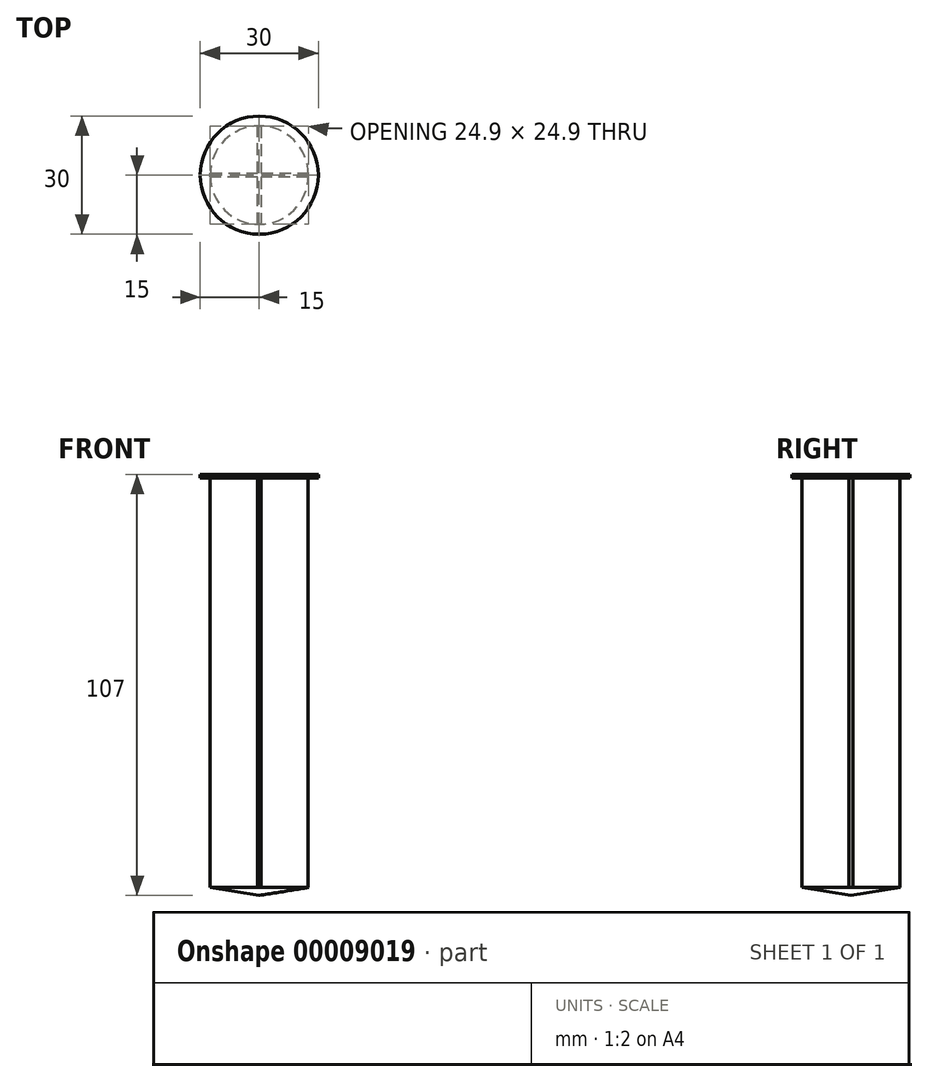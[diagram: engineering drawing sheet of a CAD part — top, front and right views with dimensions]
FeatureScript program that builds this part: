
annotation { "Feature Type Name" : "Feature", "Feature Type Description" : "" }
export const myFeature = defineFeature(function(context is Context, id is Id, definition is map)
    precondition{}
    {
        {
            var Q0;
            Q0=qCreatedBy(makeId("Top.planeOp"),FACE);
            var sketch = newSketch(context, id + "F0", { "sketchPlane" : qUnion([Q0])});
            skLineSegment(sketch, "E0", {"start": v(-0.5, 0.5) * mm, "end": v(-0.5, 12.45) * mm});
            skLineSegment(sketch, "E1", {"start": v(-0.5, 12.45) * mm, "end": v(0.5, 12.45) * mm});
            skLineSegment(sketch, "E2", {"start": v(0.5, 12.45) * mm, "end": v(0.5, 0.5) * mm});
            skLineSegment(sketch, "E3", {"start": v(0.5, 0.5) * mm, "end": v(12.45, 0.5) * mm});
            skLineSegment(sketch, "E4", {"start": v(12.45, 0.5) * mm, "end": v(12.45, -0.5) * mm});
            skLineSegment(sketch, "E5", {"start": v(12.45, -0.5) * mm, "end": v(0.5, -0.5) * mm});
            skLineSegment(sketch, "E6", {"start": v(0.5, -0.5) * mm, "end": v(0.5, -12.45) * mm});
            skLineSegment(sketch, "E7", {"start": v(0.5, -12.45) * mm, "end": v(-0.5, -12.45) * mm});
            skLineSegment(sketch, "E8", {"start": v(-0.5, -12.45) * mm, "end": v(-0.5, -0.5) * mm});
            skLineSegment(sketch, "E9", {"start": v(-0.5, -0.5) * mm, "end": v(-12.45, -0.5) * mm});
            skLineSegment(sketch, "E10", {"start": v(-12.45, -0.5) * mm, "end": v(-12.45, 0.5) * mm});
            skLineSegment(sketch, "E11", {"start": v(-12.45, 0.5) * mm, "end": v(-0.5, 0.5) * mm});
            skSolve(sketch);
        }
        {
            var Q0;
            Q0 = qSketchRegion(id + "F0", true);
            extrude(context, id + "F1", {"entities" : qUnion([Q0]), "depth" : 104 * mm});
        }
        {
            var Q0;
            Q0=qCreatedBy(makeId("Front.planeOp"),FACE);
            var sketch = newSketch(context, id + "F2", { "sketchPlane" : qUnion([Q0])});
            skLineSegment(sketch, "E12", {"start": v(0, 0) * mm, "end": v(12.5, 0) * mm});
            skLineSegment(sketch, "E13", {"start": v(12.5, 0) * mm, "end": v(0, -2) * mm});
            skLineSegment(sketch, "E14", {"start": v(0, -2) * mm, "end": v(0, 0) * mm});
            skSolve(sketch);
        }
        {
            var Q0;
            Q0 = qSketchRegion(id + "F2", true);
            var Q1;
            Q1=sQuery(id+"F2.wireOp",EDGE,"E14");
            revolve(context, id + "F3", {"operationType" : NewBodyOperationType.ADD, "entities" : qUnion([Q0]), "axis" : qUnion([Q1]), "revolveType" : RevolveType.FULL});
        }
        {
            var Q0;
            Q0=makeQuery(id+"F1.opExtrude","CAP_FACE",FACE,{"disambiguationData":[OSD([sQuery(id+"F0.wireOp",EDGE,"E0"),sQuery(id+"F0.wireOp",EDGE,"E1"),sQuery(id+"F0.wireOp",EDGE,"E2"),sQuery(id+"F0.wireOp",EDGE,"E3"),sQuery(id+"F0.wireOp",EDGE,"E4"),sQuery(id+"F0.wireOp",EDGE,"E5"),sQuery(id+"F0.wireOp",EDGE,"E6"),sQuery(id+"F0.wireOp",EDGE,"E7"),sQuery(id+"F0.wireOp",EDGE,"E8"),sQuery(id+"F0.wireOp",EDGE,"E9"),sQuery(id+"F0.wireOp",EDGE,"E10"),sQuery(id+"F0.wireOp",EDGE,"E11")])],"isStart":false});
            var sketch = newSketch(context, id + "F4", { "sketchPlane" : qUnion([Q0])});
            skCircle(sketch, "E15", {"center": v(0, 0) * mm, "radius": 15 * mm});
            skSolve(sketch);
        }
        {
            var Q0;
            Q0 = qSketchRegion(id + "F4", true);
            extrude(context, id + "F5", {"entities" : qUnion([Q0]), "operationType" : NewBodyOperationType.ADD, "depth" : 1 * mm});
        }
    });
